# Revit family: Electrical_Controls_Conspec_Fireray-3000-Transmitter-And-Receiver-Units
name_source: partatom
category: Electrical Fixtures
units: mm (PartAtom-declared; Revit-internal decimal feet)

## family parameters
Classification Number = 23.85.30.21
Cut with Voids When Loaded = No
Host = Face
Maintain Annotation Orientation = No
Part Type = Normal
Room Calculation Point = No
Round Connector Dimension = Use Diameter
Shared = No

## types (2) — shared parameters
Apparent Load = 0 VA
Assembly Code = D5030
Date Updated = 2023/10/17
Depth = 6.33 "
Height = 3.03 "
Housing = UL94 V2 PC, IP54
Keynote = 16000
Lateral Spacing = 60ft per NFPA 72
Manufacturer = CONSPEC Controls
Number of Poles = 3
Operating Humidity = 0% to 93% RH Non-Condesing
Operating Temperature = -4°F to +131°F
Operating Transmitter Current = 8 mA
Power Factor = 0.8
Product Material = Conspec - Plastic - PC - White
Product data url = https://bimobject.com
URL = https://www.conspec-controls.com
Version = 1
Voltage = 36 V
Voltage Range = 12V to 36V DC ±10%
Weight = 0.46 lbf
Width = 3.07 "
zero-valued in all types: Default Elevation

## per-type parameters (varying)
| type | Description | z_Receiver | z_Transmitter |
| Fireray 3000 Transmitter | Transmitter Unit for Fireray 3000 Smoke Detector | No | Yes |
| Fireray 3000 Receiver | Receiver Unit for Fireray 3000 Smoke Detector | Yes | No |

note: column(s) folded — value = type name in every type: Model

## geometry (parser evidence)
native form markers: Sweep x1
no freeform markers — native parametric forms only
